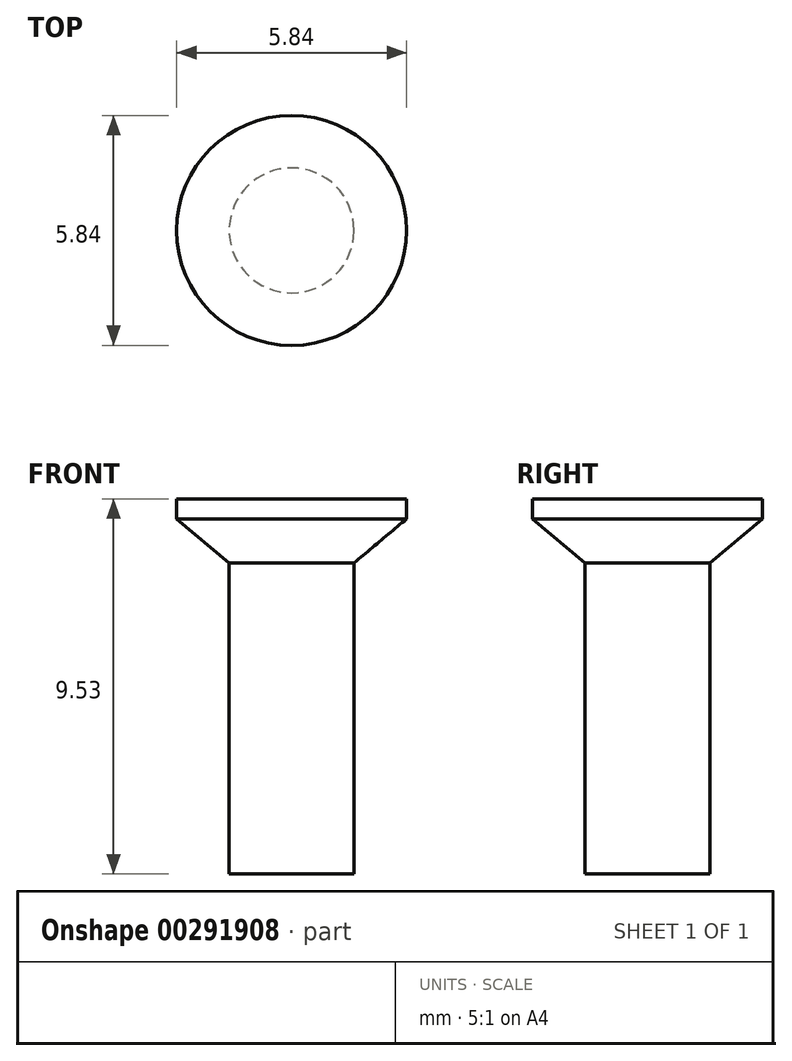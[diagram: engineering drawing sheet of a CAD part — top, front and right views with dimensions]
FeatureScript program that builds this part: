
annotation { "Feature Type Name" : "Feature", "Feature Type Description" : "" }
export const myFeature = defineFeature(function(context is Context, id is Id, definition is map)
    precondition{}
    {
        {
            var Q0;
            Q0=qCreatedBy(makeId("Front.planeOp"),FACE);
            var sketch = newSketch(context, id + "F0", { "sketchPlane" : qUnion([Q0])});
            skLineSegment(sketch, "E0", {"start": v(0, 0) * mm, "end": v(-2.92, 0) * mm});
            skLineSegment(sketch, "E1", {"start": v(-2.92, 0) * mm, "end": v(-2.92, -0.5) * mm});
            skLineSegment(sketch, "E2", {"start": v(-2.92, -0.5) * mm, "end": v(-1.59, -1.63) * mm});
            skLineSegment(sketch, "E3", {"start": v(-1.59, -1.63) * mm, "end": v(-1.59, -9.53) * mm});
            skLineSegment(sketch, "E4", {"start": v(-1.59, -9.53) * mm, "end": v(0, -9.53) * mm});
            skLineSegment(sketch, "E5", {"start": v(0, -9.53) * mm, "end": v(0, 0) * mm});
            skLineSegment(sketch, "E6", {"start": v(-2.92, -0.5) * mm, "end": v(0, -0.5) * mm, "construction": true});
            skLineSegment(sketch, "E7", {"start": v(-1.59, -1.63) * mm, "end": v(-1.59, -0.5) * mm, "construction": true});
            skLineSegment(sketch, "E8", {"start": v(0, 73.66) * mm, "end": v(0, -52.05) * mm, "construction": true});
            skSolve(sketch);
        }
        {
            var Q0;
            Q0=makeQuery(id+"F0.imprint","IMPRINT",FACE,{"disambiguationData":[TD([[makeQuery(id+"F0.imprint","IMPRINT",EDGE,{"derivedFrom":sQuery(id+"F0.wireOp",EDGE,"E0")}),1.0]])]});
            var Q1;
            Q1=sQuery(id+"F0.wireOp",EDGE,"E8");
            revolve(context, id + "F1", {"entities" : qUnion([Q0]), "axis" : qUnion([Q1]), "revolveType" : RevolveType.FULL});
        }
    });
